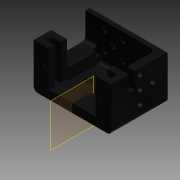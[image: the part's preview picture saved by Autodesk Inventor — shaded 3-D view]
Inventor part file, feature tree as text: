
AUTODESK INVENTOR PART (.ipt)
format: ipt  version: 2014 SP2 (Build 180246200, 246)  size: 485,376 bytes
history: native  units: in
note: dims shown in document units (in); Inventor stores cm internally (conversion verified against a paired STEP export)
features: sketch x24, extrude x21, reference x11, plane x9, mirror x5, projected_geometry x3, pattern_circular x2, fillet x1
ambient origin geometry x8: Origin, YZ Plane, XZ Plane, XY Plane, X Axis, Y Axis, Z Axis, Center Point
bodies: Solid1 (feature_tree)
feature tree (76):
  sketch  "Sketch2"  dims[d0=0.198in d1=0.1705in]
  extrude  "Extrusion1"  Depth=0.1705in
  extrude  "Extrusion2"  Depth=0.1in
  extrude  "Extrusion3"  Depth=0.1181in
  extrude  "Extrusion4"  Depth=0.1181in
  mirror  "Mirror1"
  extrude  "Extrusion6"  Depth=0.1575in
  plane  "Work Plane1"
  extrude  "Extrusion10"  Depth=0.3937in TaperAngle=0.0deg
  extrude  "Extrusion11"  Depth=0.0984in TaperAngle=0.0deg
  sketch  "Sketch15"  dims[d36=0.7874in d37=0.0in d38=0.1in]
  extrude  "Extrusion13"  Depth=0.2362in TaperAngle=0.0deg
  extrude  "Extrusion14"  Depth=0.1in
  pattern_circular  "Circular Pattern1"  Count=4 Angle=360.0deg
  sketch  "Sketch16"  dims[d39=0.748in d40=0.0in]
  sketch  "Sketch18"  dims[d50=0.5118in]
  extrude  "Extrusion17"  Depth=0.0118in
  plane  "Work Plane3"
  mirror  "Mirror5"
  extrude  "Extrusion21"  Depth=0.0118in
  extrude  "Extrusion22"  Depth=0.1181in
  plane  "Work Plane4"
  mirror  "Mirror6"
  extrude  "Extrusion25"  Depth=0.0394in TaperAngle=0.0deg
  pattern_circular  "Circular Pattern4"  Count=4 Angle=360.0deg
  plane  "Work Plane5"
  extrude  "Extrusion29"  TaperAngle=45.0deg  [1 undecoded]
  sketch  "Sketch35"  dims[d64=0.0118in d65=0.0118in]
  plane  "Work Plane6"
  extrude  "Extrusion31"  Depth=0.3937in
  sketch  "Sketch37"  dims[d74=0.0in d75=0.0in d89=0.0394in d90=0.0in]
  extrude  "Extrusion33"  Depth=0.0984in
  extrude  "Extrusion34"  Depth=0.0787in TaperAngle=0.0deg
  extrude  "Extrusion35"  Depth=0.6693in
  fillet  "Fillet2"  Radius=0.315in
  plane  "Work Plane7"
  plane  "Work Plane8"
  extrude  "Extrusion38"  Depth=0.1575in TaperAngle=0.0deg
  plane  "Work Plane9"
  plane  "Work Plane10"
  extrude  "Extrusion39"  Depth=0.1575in TaperAngle=0.0deg
  mirror  "Mirror10"
  extrude  "Extrusion40"  Depth=0.1969in
  mirror  "Mirror11"
  sketch  "Sketch3"  dims[d2=0.1in d3=0.9039in]
  sketch  "Sketch4"  dims[d4=0.8921in d5=0.1181in]
  projected_geometry  "Projected Loop1"
  sketch  "Sketch5"  dims[d6=0.1181in d7=0.1181in]
  projected_geometry  "Projected Loop2"
  sketch  "Sketch6"  dims[d8=0.3543in d9=0.1575in]
  reference  "Reference1"
  reference  "Reference2"
  sketch  "Sketch8"  dims[d10=0.315in d11=0.3937in d12=0.0in]
  projected_geometry  "Projected Loop3"
  sketch  "Sketch12"  dims[d13=0.3937in d14=0.0in d15=0.0984in d16=0.0in]
  sketch  "Sketch13"  dims[d17=0.2362in d18=0.0in d24=0.063in d25=0.0in]
  reference  "Reference5"
  sketch  "Sketch19"  dims[d51=0.1299in]
  sketch  "Sketch23"  dims[d52=0.1299in]
  sketch  "Sketch24"  dims[d53=0.748in d54=0.0in]
  sketch  "Sketch28"  dims[d55=0.748in d56=0.0in d57=1.5748in d58=360.0deg]
  reference  "Reference9"
  sketch  "Sketch33"  dims[d60=0.5512in d62=0.0118in]
  sketch  "Sketch36"  dims[d70=0.1181in d71=0.0236in]
  reference  "Reference13"
  reference  "Reference14"
  reference  "Reference15"
  reference  "Reference16"
  reference  "Reference17"
  sketch  "Sketch38"  dims[d91=0.0394in d92=0.0in]
  sketch  "Sketch39"  dims[d107=0.1181in]
  sketch  "Sketch43"  dims[d108=0.1181in]
  sketch  "Sketch44"  dims[d109=0.5118in]
  reference  "Reference18"
  reference  "Reference19"
  sketch  "Sketch45"  dims[d110=0.3937in d111=0.0in d112=1.5748in d113=360.0deg d125=45.0deg d132=0.374in d133=0.0984in d134=0.0787in d135=0.0in d138=0.6693in d139=0.315in d140=0.0in d143=0.1575in d144=0.0in d145=0.1575in d146=0.0in d147=0.1969in d148=0.1575in d149=0.0in d150=0.0787in d162=0.2362in d163=0.3937in d164=0.0in d165=0.0787in d166=0.3937in d167=0.0in d168=0.0394in d169=0.3937in d170=0.0in]
note: 1 required parameter value undecoded (feature->parameter linkage not recoverable at this tier; creation-order binding heuristic only, values carry confidence <= 0.55)
